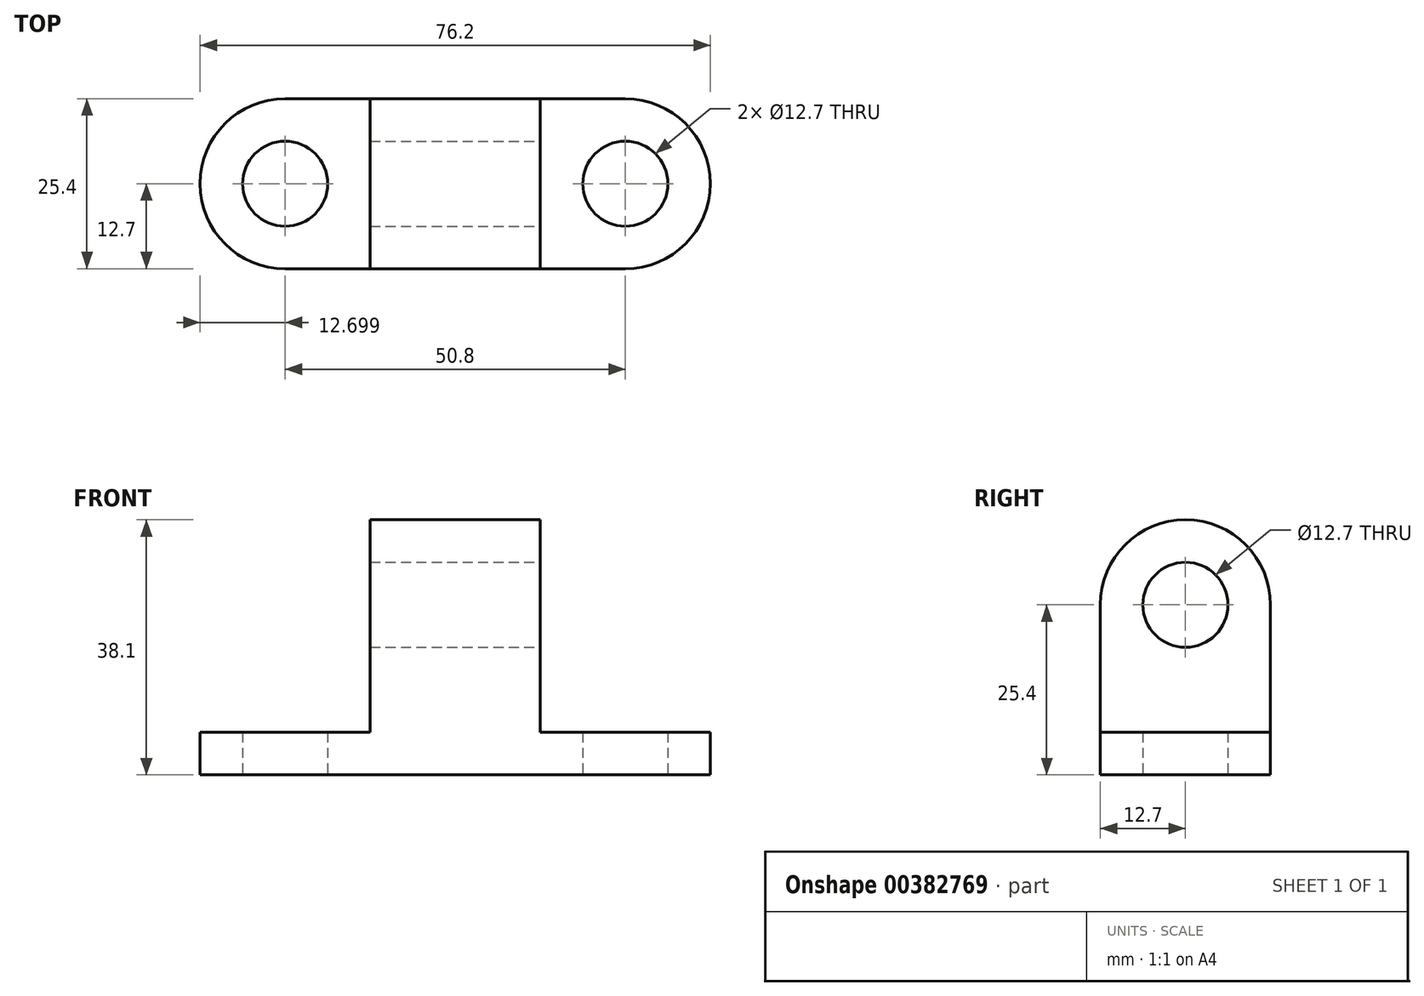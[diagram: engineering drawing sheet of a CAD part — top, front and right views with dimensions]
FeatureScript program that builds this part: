
annotation { "Feature Type Name" : "Feature", "Feature Type Description" : "" }
export const myFeature = defineFeature(function(context is Context, id is Id, definition is map)
    precondition{}
    {
        {
            var Q0;
            Q0=qCreatedBy(makeId("Front.planeOp"),FACE);
            var sketch = newSketch(context, id + "F0", { "sketchPlane" : qUnion([Q0])});
            skLineSegment(sketch, "E0.bottom", {"start": v(22.85, 0) * mm, "end": v(-53.35, 0) * mm});
            skLineSegment(sketch, "E0.top", {"start": v(22.85, 38.1) * mm, "end": v(-53.35, 38.1) * mm});
            skLineSegment(sketch, "E0.left", {"start": v(22.85, 0) * mm, "end": v(22.85, 38.1) * mm});
            skLineSegment(sketch, "E0.right", {"start": v(-53.35, 0) * mm, "end": v(-53.35, 38.1) * mm});
            skSolve(sketch);
        }
        {
            var Q0;
            Q0=makeQuery(id+"F0.imprint","IMPRINT",FACE,{"disambiguationData":[TD([[makeQuery(id+"F0.imprint","IMPRINT",EDGE,{"derivedFrom":sQuery(id+"F0.wireOp",EDGE,"E0.bottom")}),-1.0]])]});
            extrude(context, id + "F1", {"entities" : qUnion([Q0]), "depth" : 25.4 * mm});
        }
        {
            var Q0;
            Q0=makeQuery(id+"F1.opExtrude","CAP_FACE",FACE,{"disambiguationData":[OSD([sQuery(id+"F0.wireOp",EDGE,"E0.bottom"),sQuery(id+"F0.wireOp",EDGE,"E0.top"),sQuery(id+"F0.wireOp",EDGE,"E0.left"),sQuery(id+"F0.wireOp",EDGE,"E0.right")])],"isStart":false});
            var sketch = newSketch(context, id + "F2", { "sketchPlane" : qUnion([Q0])});
            skLineSegment(sketch, "E1", {"start": v(-2.55, 38.1) * mm, "end": v(-2.55, 6.35) * mm});
            skLineSegment(sketch, "E2", {"start": v(-2.55, 6.35) * mm, "end": v(22.85, 6.35) * mm});
            skLineSegment(sketch, "E3", {"start": v(22.85, 6.35) * mm, "end": v(22.85, 38.1) * mm});
            skLineSegment(sketch, "E4", {"start": v(22.85, 38.1) * mm, "end": v(-2.55, 38.1) * mm});
            skLineSegment(sketch, "E5", {"start": v(-53.35, 6.35) * mm, "end": v(-53.35, 38.1) * mm});
            skLineSegment(sketch, "E6", {"start": v(-53.35, 38.1) * mm, "end": v(-27.95, 38.1) * mm});
            skLineSegment(sketch, "E7", {"start": v(-27.95, 38.1) * mm, "end": v(-27.95, 6.35) * mm});
            skLineSegment(sketch, "E8", {"start": v(-27.95, 6.35) * mm, "end": v(-53.35, 6.35) * mm});
            skSolve(sketch);
        }
        {
            var Q0;
            Q0=makeQuery(id+"F2.imprint","IMPRINT",FACE,{"disambiguationData":[TD([[makeQuery(id+"F2.imprint","IMPRINT",EDGE,{"derivedFrom":sQuery(id+"F2.wireOp",EDGE,"E5")}),-1.0]])]});
            var Q1;
            Q1=makeQuery(id+"F2.imprint","IMPRINT",FACE,{"disambiguationData":[TD([[makeQuery(id+"F2.imprint","IMPRINT",EDGE,{"derivedFrom":sQuery(id+"F2.wireOp",EDGE,"E1")}),1.0]])]});
            extrude(context, id + "F3", {"entities" : qUnion([Q0, Q1]), "operationType" : NewBodyOperationType.REMOVE, "oppositeDirection" : true, "depth" : 31.75 * mm});
        }
        {
            var Q0;
            Q0=qCreatedBy(makeId("Top.planeOp"),FACE);
            var sketch = newSketch(context, id + "F4", { "sketchPlane" : qUnion([Q0])});
            skCircle(sketch, "E9", {"center": v(10.15, -12.7) * mm, "radius": 6.35 * mm});
            skCircle(sketch, "E10", {"center": v(-40.65, -12.7) * mm, "radius": 6.35 * mm});
            skArc(sketch, "E11", {"start": v(-40.65, 0) * mm, "mid": v(-49.63, -3.72) * mm, "end": v(-53.35, -12.7) * mm});
            skArc(sketch, "E12", {"start": v(-53.35, -12.7) * mm, "mid": v(-49.63, -21.68) * mm, "end": v(-40.65, -25.4) * mm});
            skArc(sketch, "E13", {"start": v(22.85, -12.7) * mm, "mid": v(19.13, -3.72) * mm, "end": v(10.15, 0) * mm});
            skArc(sketch, "E14", {"start": v(10.15, -25.4) * mm, "mid": v(19.13, -21.68) * mm, "end": v(22.85, -12.7) * mm});
            skLineSegment(sketch, "E15", {"start": v(-53.35, -12.7) * mm, "end": v(-53.35, 0) * mm});
            skLineSegment(sketch, "E16", {"start": v(-53.35, 0) * mm, "end": v(-40.65, 0) * mm});
            skLineSegment(sketch, "E17", {"start": v(-53.35, -12.7) * mm, "end": v(-53.35, -25.54) * mm});
            skLineSegment(sketch, "E18", {"start": v(-53.35, -25.54) * mm, "end": v(-40.65, -25.4) * mm});
            skLineSegment(sketch, "E19", {"start": v(10.15, 0) * mm, "end": v(22.85, 0) * mm});
            skLineSegment(sketch, "E20", {"start": v(22.85, 0) * mm, "end": v(22.85, -12.7) * mm});
            skLineSegment(sketch, "E21", {"start": v(22.85, -12.7) * mm, "end": v(22.85, -25.4) * mm});
            skLineSegment(sketch, "E22", {"start": v(22.85, -25.4) * mm, "end": v(10.15, -25.4) * mm});
            skSolve(sketch);
        }
        {
            var Q0;
            Q0 = qSketchRegion(id + "F4", true);
            extrude(context, id + "F5", {"entities" : qUnion([Q0]), "operationType" : NewBodyOperationType.REMOVE, "depth" : 25.4 * mm});
        }
        {
            var Q0;
            Q0=makeQuery(id+"F3.boolean.opBoolean","COPY",FACE,{"derivedFrom":makeQuery(id+"F3.opExtrude","SWEPT_FACE",FACE,{"disambiguationData":[OSD([sQuery(id+"F2.wireOp",EDGE,"E1")])]})});
            var sketch = newSketch(context, id + "F6", { "sketchPlane" : qUnion([Q0])});
            skPoint(sketch, "E23.centerSnap0", {"position": v(-12.7, 38.1) * mm});
            skCircle(sketch, "E24", {"center": v(-12.7, 25.4) * mm, "radius": 6.35 * mm});
            skArc(sketch, "E25", {"start": v(-12.7, 38.1) * mm, "mid": v(-21.68, 34.38) * mm, "end": v(-25.4, 25.4) * mm});
            skArc(sketch, "E26", {"start": v(0, 25.4) * mm, "mid": v(-3.72, 34.38) * mm, "end": v(-12.7, 38.1) * mm});
            skLineSegment(sketch, "E27", {"start": v(-25.4, 25.4) * mm, "end": v(-25.4, 38.1) * mm});
            skLineSegment(sketch, "E28", {"start": v(-25.4, 38.1) * mm, "end": v(-12.7, 38.1) * mm});
            skLineSegment(sketch, "E29", {"start": v(-12.7, 38.1) * mm, "end": v(0, 38.1) * mm});
            skLineSegment(sketch, "E30", {"start": v(0, 38.1) * mm, "end": v(0, 25.4) * mm});
            skSolve(sketch);
        }
        {
            var Q0;
            Q0 = qSketchRegion(id + "F6", true);
            extrude(context, id + "F7", {"entities" : qUnion([Q0]), "operationType" : NewBodyOperationType.REMOVE, "oppositeDirection" : true, "depth" : 31.75 * mm});
        }
    });
